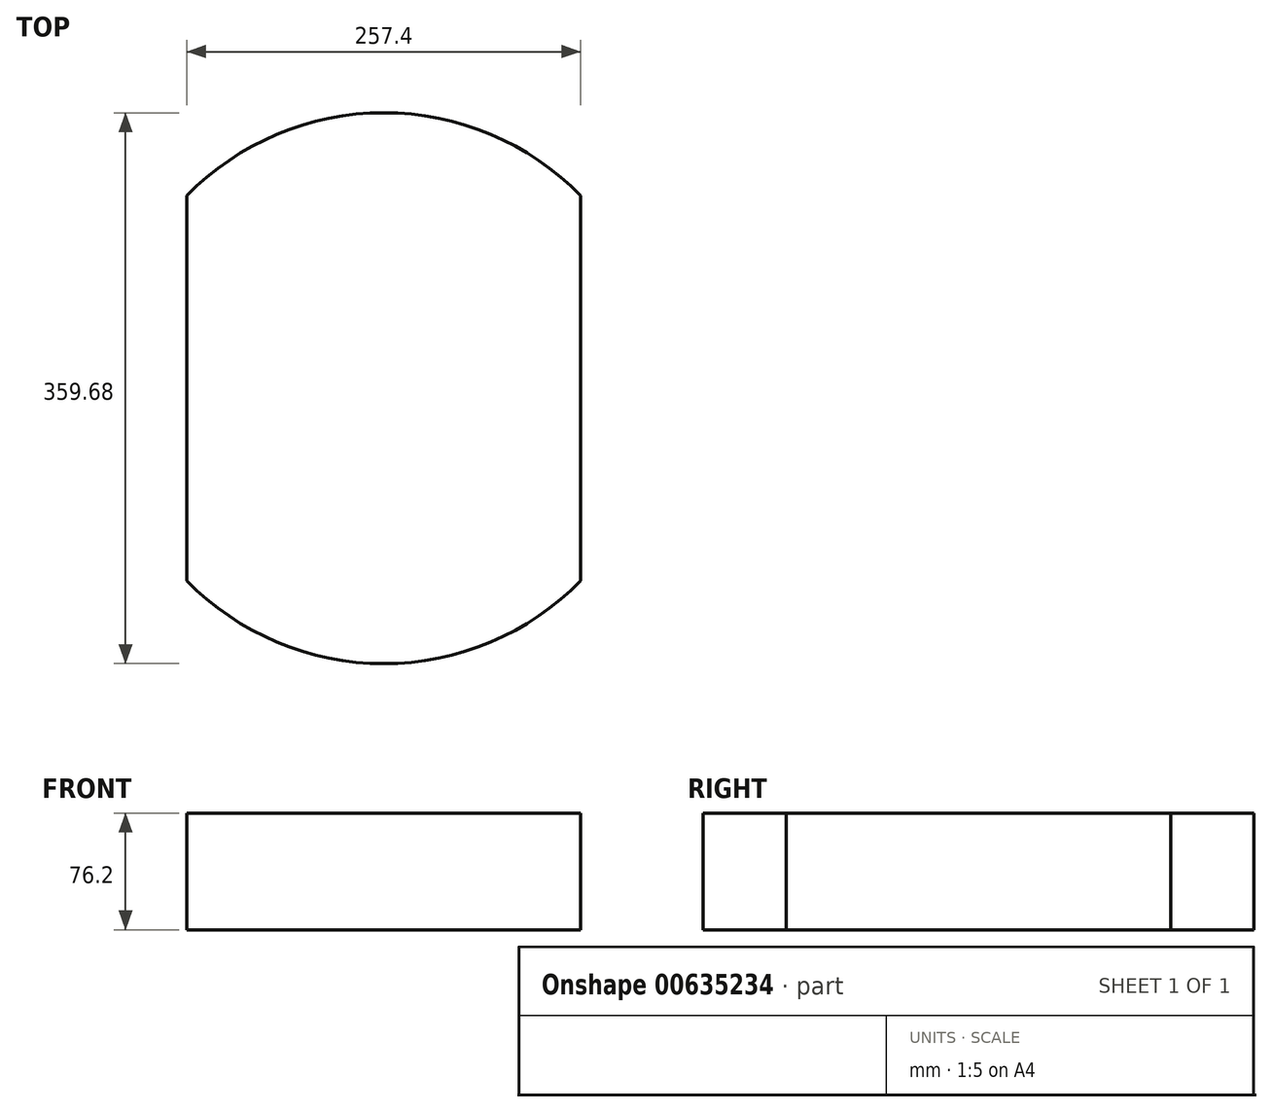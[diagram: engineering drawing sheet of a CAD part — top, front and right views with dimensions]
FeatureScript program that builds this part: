
annotation { "Feature Type Name" : "Feature", "Feature Type Description" : "" }
export const myFeature = defineFeature(function(context is Context, id is Id, definition is map)
    precondition{}
    {
        {
            var Q0;
            Q0=qCreatedBy(makeId("Top.planeOp"),FACE);
            var sketch = newSketch(context, id + "F0", { "sketchPlane" : qUnion([Q0])});
            skCircle(sketch, "E0", {"center": v(0, 0) * mm, "radius": 179.84 * mm});
            skLineSegment(sketch, "E1.bottom", {"start": v(-128.7, 125.62) * mm, "end": v(128.7, 125.62) * mm});
            skLineSegment(sketch, "E1.top", {"start": v(-128.7, -125.62) * mm, "end": v(128.7, -125.62) * mm});
            skLineSegment(sketch, "E1.left", {"start": v(-128.7, 125.62) * mm, "end": v(-128.7, -125.62) * mm});
            skLineSegment(sketch, "E1.right", {"start": v(128.7, 125.62) * mm, "end": v(128.7, -125.62) * mm});
            skSolve(sketch);
        }
        {
            var Q0;
            {var subQ0=sQuery(id+"F0.wireOp",EDGE,"E1.top");Q0=makeQuery(id+"F0.imprint","IMPRINT",FACE,{"disambiguationData":[TD([[makeQuery(id+"F0.imprint","IMPRINT",EDGE,{"derivedFrom":subQ0}),-1.0]])]});}
            var Q1;
            Q1=makeQuery(id+"F0.imprint","IMPRINT",FACE,{"disambiguationData":[TD([[makeQuery(id+"F0.imprint","IMPRINT",EDGE,{"derivedFrom":sQuery(id+"F0.wireOp",EDGE,"E1.bottom")}),-1.0]])]});
            var Q2;
            {var subQ0=sQuery(id+"F0.wireOp",EDGE,"E1.bottom");Q2=makeQuery(id+"F0.imprint","IMPRINT",FACE,{"disambiguationData":[TD([[makeQuery(id+"F0.imprint","IMPRINT",EDGE,{"derivedFrom":subQ0}),1.0]])]});}
            extrude(context, id + "F1", {"entities" : qUnion([Q0, Q1, Q2]), "depth" : 76.2 * mm, "offsetDistance" : 25.4 * mm});
        }
    });
